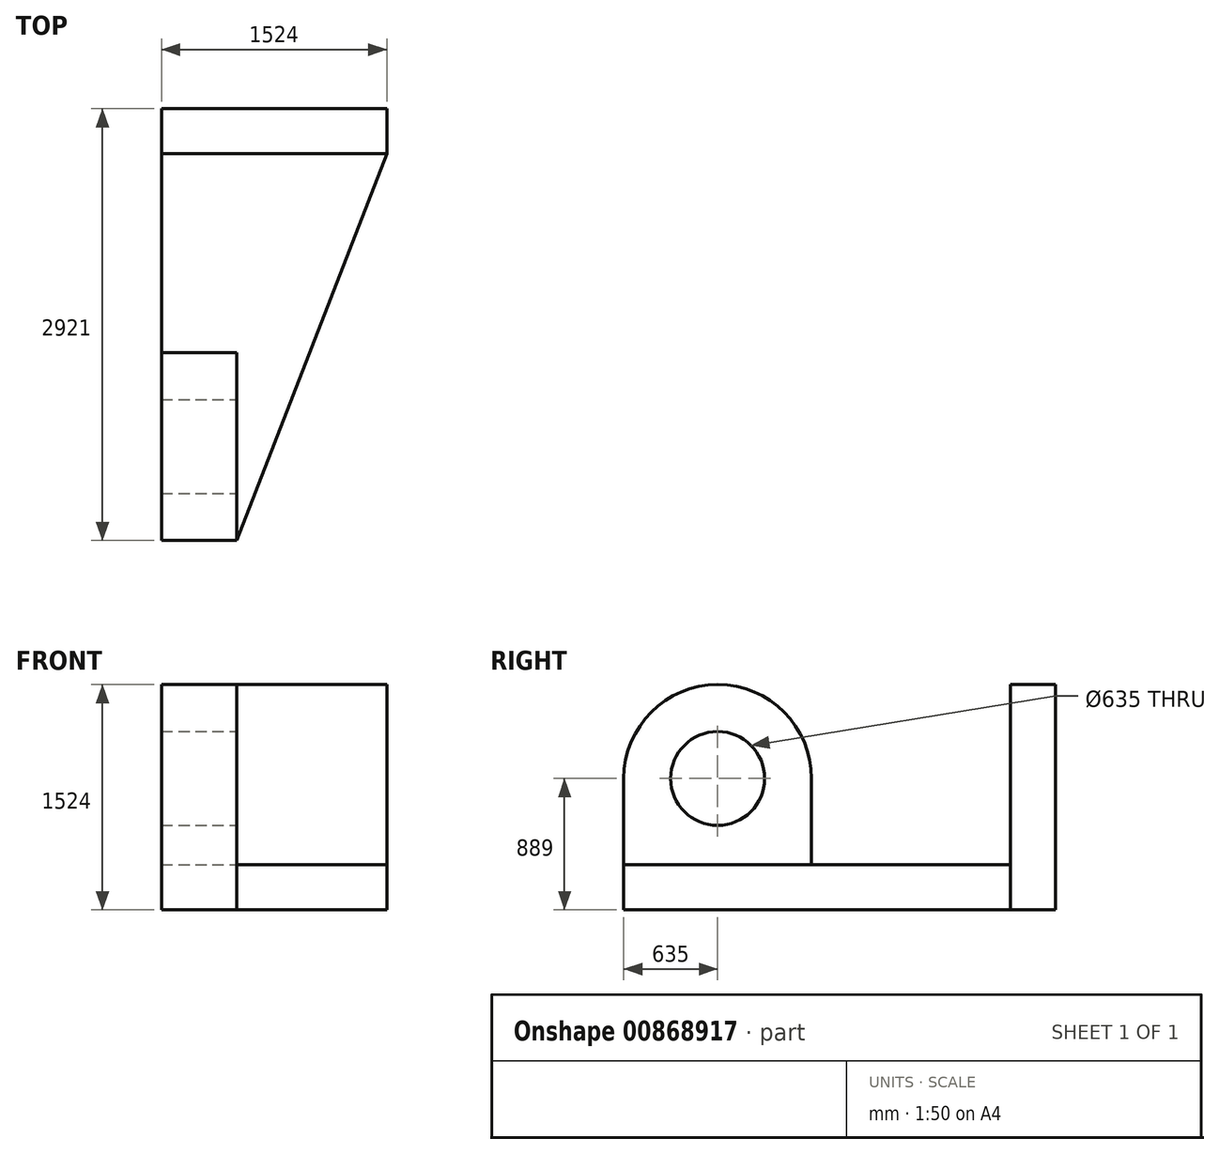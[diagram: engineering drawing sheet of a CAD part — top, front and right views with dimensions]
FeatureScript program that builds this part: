
annotation { "Feature Type Name" : "Feature", "Feature Type Description" : "" }
export const myFeature = defineFeature(function(context is Context, id is Id, definition is map)
    precondition{}
    {
        {
            var Q0;
            Q0=qCreatedBy(makeId("Front.planeOp"),FACE);
            var sketch = newSketch(context, id + "F0", { "sketchPlane" : qUnion([Q0])});
            skLineSegment(sketch, "E0.bottom", {"start": v(-762, 762) * mm, "end": v(762, 762) * mm});
            skLineSegment(sketch, "E0.top", {"start": v(-762, -762) * mm, "end": v(762, -762) * mm});
            skLineSegment(sketch, "E0.left", {"start": v(-762, 762) * mm, "end": v(-762, -762) * mm});
            skLineSegment(sketch, "E0.right", {"start": v(762, 762) * mm, "end": v(762, -762) * mm});
            skPoint(sketch, "E0.middle", {"position": v(0, 0) * mm});
            skSolve(sketch);
        }
        {
            var Q0;
            Q0=makeQuery(id+"F0.imprint","IMPRINT",FACE,{"disambiguationData":[TD([[makeQuery(id+"F0.imprint","IMPRINT",EDGE,{"derivedFrom":sQuery(id+"F0.wireOp",EDGE,"E0.bottom")}),-1.0]])]});
            extrude(context, id + "F1", {"entities" : qUnion([Q0]), "depth" : 304.8 * mm, "offsetDistance" : 25.4 * mm});
        }
        {
            var Q0;
            Q0=makeQuery(id+"F1.opExtrude","CAP_FACE",FACE,{"disambiguationData":[OSD([sQuery(id+"F0.wireOp",EDGE,"E0.bottom"),sQuery(id+"F0.wireOp",EDGE,"E0.top"),sQuery(id+"F0.wireOp",EDGE,"E0.left"),sQuery(id+"F0.wireOp",EDGE,"E0.right")])],"isStart":true});
            var sketch = newSketch(context, id + "F2", { "sketchPlane" : qUnion([Q0])});
            skLineSegment(sketch, "E1.bottom", {"start": v(-762, -762) * mm, "end": v(762, -762) * mm});
            skLineSegment(sketch, "E1.top", {"start": v(-762, -457.2) * mm, "end": v(762, -457.2) * mm});
            skLineSegment(sketch, "E1.left", {"start": v(-762, -762) * mm, "end": v(-762, -457.2) * mm});
            skLineSegment(sketch, "E1.right", {"start": v(762, -762) * mm, "end": v(762, -457.2) * mm});
            skSolve(sketch);
        }
        {
            var Q0;
            Q0=makeQuery(id+"F2.imprint","IMPRINT",FACE,{"disambiguationData":[TD([[makeQuery(id+"F2.imprint","IMPRINT",EDGE,{"derivedFrom":sQuery(id+"F2.wireOp",EDGE,"E1.bottom")}),-1.0]])]});
            extrude(context, id + "F3", {"entities" : qUnion([Q0]), "operationType" : NewBodyOperationType.ADD, "oppositeDirection" : true, "depth" : 2921 * mm, "offsetDistance" : 25.4 * mm});
        }
        {
            var Q0;
            Q0=makeQuery(id+"F3.opExtrude","SWEPT_FACE",FACE,{"disambiguationData":[OSD([sQuery(id+"F2.wireOp",EDGE,"E1.top")])]});
            var sketch = newSketch(context, id + "F4", { "sketchPlane" : qUnion([Q0])});
            skLineSegment(sketch, "E2.bottom", {"start": v(-762, -2921) * mm, "end": v(-254, -2921) * mm});
            skLineSegment(sketch, "E2.top", {"start": v(-762, -1651) * mm, "end": v(-254, -1651) * mm});
            skLineSegment(sketch, "E2.left", {"start": v(-762, -2921) * mm, "end": v(-762, -1651) * mm});
            skLineSegment(sketch, "E2.right", {"start": v(-254, -2921) * mm, "end": v(-254, -1651) * mm});
            skSolve(sketch);
        }
        {
            var Q0;
            Q0=makeQuery(id+"F4.imprint","IMPRINT",FACE,{"disambiguationData":[TD([[makeQuery(id+"F4.imprint","IMPRINT",EDGE,{"derivedFrom":sQuery(id+"F4.wireOp",EDGE,"E2.bottom")}),-1.0]])]});
            extrude(context, id + "F5", {"entities" : qUnion([Q0]), "operationType" : NewBodyOperationType.ADD, "depth" : 584.2 * mm, "offsetDistance" : 25.4 * mm});
        }
        {
            var Q0;
            Q0=makeQuery(id+"F5.opExtrude","SWEPT_FACE",FACE,{"disambiguationData":[OSD([sQuery(id+"F4.wireOp",EDGE,"E2.right")])]});
            var sketch = newSketch(context, id + "F6", { "sketchPlane" : qUnion([Q0])});
            skCircle(sketch, "E3", {"center": v(-2286, 127) * mm, "radius": 635 * mm});
            skSolve(sketch);
        }
        {
            var Q0;
            {var subQ1=sQuery(id+"F4.wireOp",EDGE,"E2.right");var subQ2=makeQuery(id+"F5.opExtrude","CAP_EDGE",EDGE,{"disambiguationData":[OSD([subQ1])],"isStart":false});Q0=makeQuery(id+"F6.imprint","IMPRINT",FACE,{"disambiguationData":[TD([[makeQuery(id+"F6.imprint","IMPRINT",EDGE,{"derivedFrom":subQ2}),1.0]])]});}
            extrude(context, id + "F7", {"entities" : qUnion([Q0]), "operationType" : NewBodyOperationType.ADD, "oppositeDirection" : true, "depth" : 508 * mm, "offsetDistance" : 25.4 * mm});
        }
        {
            var Q0;
            {var subQ0=sQuery(id+"F4.wireOp",EDGE,"E2.right");Q0=makeQuery(id+"F7.boolean.opBoolean","MERGE",FACE,{"derivedFrom":[makeQuery(id+"F5.opExtrude","SWEPT_FACE",FACE,{"disambiguationData":[OSD([subQ0])]}),makeQuery(id+"F7.opExtrude","CAP_FACE",FACE,{"disambiguationData":[OSD([subQ0,sQuery(id+"F6.wireOp",EDGE,"E3")])],"isStart":true})]});}
            var sketch = newSketch(context, id + "F8", { "sketchPlane" : qUnion([Q0])});
            skCircle(sketch, "E4", {"center": v(-2286, 127) * mm, "radius": 317.5 * mm});
            skSolve(sketch);
        }
        {
            var Q0;
            Q0=makeQuery(id+"F8.imprint","IMPRINT",FACE,{"disambiguationData":[TD([[makeQuery(id+"F8.imprint","IMPRINT",EDGE,{"derivedFrom":sQuery(id+"F8.wireOp",EDGE,"E4")}),1.0]])]});
            extrude(context, id + "F9", {"entities" : qUnion([Q0]), "operationType" : NewBodyOperationType.REMOVE, "oppositeDirection" : true, "depth" : 1529.08 * mm, "offsetDistance" : 25.4 * mm});
        }
        {
            var Q0;
            Q0=makeQuery(id+"F3.opExtrude","SWEPT_FACE",FACE,{"disambiguationData":[OSD([sQuery(id+"F2.wireOp",EDGE,"E1.top")])]});
            var sketch = newSketch(context, id + "F10", { "sketchPlane" : qUnion([Q0])});
            skLineSegment(sketch, "E5", {"start": v(-254, -2921) * mm, "end": v(762, -304.8) * mm});
            skLineSegment(sketch, "E6", {"start": v(762, -304.8) * mm, "end": v(762, -2921) * mm});
            skLineSegment(sketch, "E7", {"start": v(762, -2921) * mm, "end": v(-254, -2921) * mm});
            skSolve(sketch);
        }
        {
            var Q0;
            Q0=makeQuery(id+"F10.imprint","IMPRINT",FACE,{"disambiguationData":[TD([[makeQuery(id+"F10.imprint","IMPRINT",EDGE,{"derivedFrom":sQuery(id+"F10.wireOp",EDGE,"E5")}),-1.0]])]});
            extrude(context, id + "F11", {"entities" : qUnion([Q0]), "operationType" : NewBodyOperationType.REMOVE, "oppositeDirection" : true, "depth" : 2491.74 * mm, "offsetDistance" : 25.4 * mm});
        }
    });
